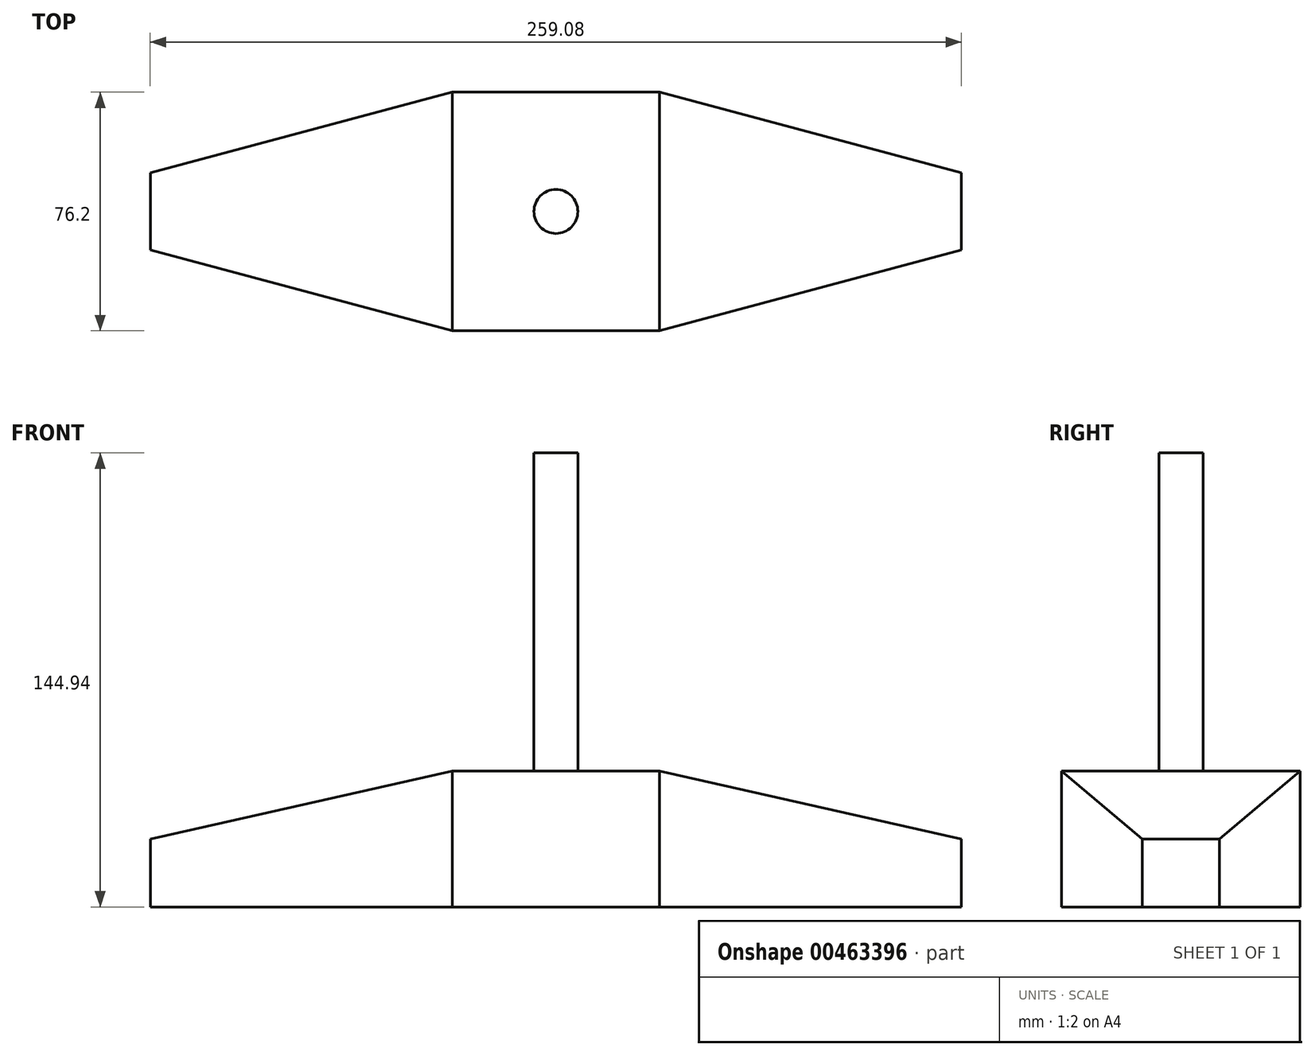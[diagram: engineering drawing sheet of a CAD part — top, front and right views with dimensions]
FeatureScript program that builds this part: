
annotation { "Feature Type Name" : "Feature", "Feature Type Description" : "" }
export const myFeature = defineFeature(function(context is Context, id is Id, definition is map)
    precondition{}
    {
        {
            var Q0;
            Q0=qCreatedBy(makeId("Front.planeOp"),FACE);
            var sketch = newSketch(context, id + "F0", { "sketchPlane" : qUnion([Q0])});
            skLineSegment(sketch, "E0.bottom", {"start": v(33.12, 21.67) * mm, "end": v(-33.12, 21.67) * mm});
            skLineSegment(sketch, "E0.top", {"start": v(129.54, -21.67) * mm, "end": v(-129.54, -21.67) * mm});
            skLineSegment(sketch, "E0.left", {"start": v(129.54, 0) * mm, "end": v(129.54, -21.67) * mm});
            skLineSegment(sketch, "E0.right", {"start": v(-129.54, 0) * mm, "end": v(-129.54, -21.67) * mm});
            skPoint(sketch, "E0.middle", {"position": v(0, 0) * mm});
            skLineSegment(sketch, "E1", {"start": v(-129.54, 0) * mm, "end": v(-33.12, 21.67) * mm});
            skLineSegment(sketch, "E2.MirrorCS", {"start": v(129.54, 0) * mm, "end": v(33.12, 21.67) * mm});
            skPoint(sketch, "E3.orphan", {"position": v(-129.54, 21.67) * mm});
            skPoint(sketch, "E4.orphan", {"position": v(129.54, 21.67) * mm});
            skLineSegment(sketch, "E5.bottom", {"start": v(0, 21.67) * mm, "end": v(14.6, 21.67) * mm});
            skLineSegment(sketch, "E5.top", {"start": v(0, 95.7) * mm, "end": v(14.6, 95.7) * mm});
            skLineSegment(sketch, "E5.left", {"start": v(0, 21.67) * mm, "end": v(0, 95.7) * mm});
            skLineSegment(sketch, "E5.right", {"start": v(14.6, 21.67) * mm, "end": v(14.6, 95.7) * mm});
            skSolve(sketch);
        }
        {
            var Q0;
            Q0=makeQuery(id+"F0.imprint","IMPRINT",FACE,{"disambiguationData":[TD([[makeQuery(id+"F0.imprint","IMPRINT",EDGE,{"derivedFrom":sQuery(id+"F0.wireOp",EDGE,"E0.top")}),-1.0]])]});
            extrude(context, id + "F1", {"entities" : qUnion([Q0]), "depth" : 76.2 * mm});
        }
        {
            var Q0;
            Q0=makeQuery(id+"F1.opExtrude","SWEPT_FACE",FACE,{"disambiguationData":[OSD([sQuery(id+"F0.wireOp",EDGE,"E0.bottom"),sQuery(id+"F0.wireOp",EDGE,"E5.bottom")])]});
            var sketch = newSketch(context, id + "F2", { "sketchPlane" : qUnion([Q0])});
            skPoint(sketch, "E6", {"position": v(0, -38.1) * mm});
            skPoint(sketch, "E6.positionSnap0", {"position": v(-33.12, -38.1) * mm});
            skPoint(sketch, "E6.positionSnap1", {"position": v(0, -76.2) * mm});
            skCircle(sketch, "E7", {"center": v(0, -38.1) * mm, "radius": 7.01 * mm});
            skSolve(sketch);
        }
        {
            var Q0;
            Q0=makeQuery(id+"F2.imprint","IMPRINT",FACE,{"disambiguationData":[TD([[makeQuery(id+"F2.imprint","IMPRINT",EDGE,{"derivedFrom":sQuery(id+"F2.wireOp",EDGE,"E7")}),1.0]])]});
            extrude(context, id + "F3", {"entities" : qUnion([Q0]), "operationType" : NewBodyOperationType.ADD, "depth" : 101.6 * mm});
        }
        {
            var Q0;
            Q0=makeQuery(id+"F1.opExtrude","SWEPT_FACE",FACE,{"disambiguationData":[OSD([sQuery(id+"F0.wireOp",EDGE,"E0.bottom"),sQuery(id+"F0.wireOp",EDGE,"E5.bottom")])]});
            var sketch = newSketch(context, id + "F4", { "sketchPlane" : qUnion([Q0])});
            skLineSegment(sketch, "E8", {"start": v(33.12, 0) * mm, "end": v(134.8, -27.2) * mm});
            skLineSegment(sketch, "E9", {"start": v(134.8, -27.2) * mm, "end": v(134.8, 6.29) * mm});
            skLineSegment(sketch, "E10", {"start": v(134.8, 6.29) * mm, "end": v(33.12, 0) * mm});
            skLineSegment(sketch, "E11.MirrorCS", {"start": v(-33.12, 0) * mm, "end": v(-134.8, -27.2) * mm});
            skLineSegment(sketch, "E12.MirrorCS", {"start": v(-134.8, 6.29) * mm, "end": v(-33.12, 0) * mm});
            skLineSegment(sketch, "E13.MirrorCS", {"start": v(-134.8, -27.2) * mm, "end": v(-134.8, 6.29) * mm});
            skLineSegment(sketch, "E14.MirrorCS", {"start": v(33.12, -76.2) * mm, "end": v(134.8, -49) * mm});
            skLineSegment(sketch, "E15.MirrorCS", {"start": v(134.8, -82.49) * mm, "end": v(33.12, -76.2) * mm});
            skLineSegment(sketch, "E16.MirrorCS", {"start": v(134.8, -49) * mm, "end": v(134.8, -82.49) * mm});
            skLineSegment(sketch, "E17.MirrorCS", {"start": v(-33.12, -76.2) * mm, "end": v(-134.8, -49) * mm});
            skLineSegment(sketch, "E18.MirrorCS", {"start": v(-134.8, -82.49) * mm, "end": v(-33.12, -76.2) * mm});
            skLineSegment(sketch, "E19.MirrorCS", {"start": v(-134.8, -49) * mm, "end": v(-134.8, -82.49) * mm});
            skSolve(sketch);
        }
        {
            var Q0;
            Q0=makeQuery(id+"F4.imprint","IMPRINT",FACE,{"disambiguationData":[TD([[makeQuery(id+"F4.imprint","IMPRINT",EDGE,{"derivedFrom":sQuery(id+"F4.wireOp",EDGE,"E8")}),1.0]])]});
            extrude(context, id + "F5", {"entities" : qUnion([Q0]), "operationType" : NewBodyOperationType.REMOVE, "oppositeDirection" : true, "depth" : 76.2 * mm});
        }
        {
            var Q0;
            Q0 = qSketchRegion(id + "F4", true);
            extrude(context, id + "F6", {"entities" : qUnion([Q0]), "operationType" : NewBodyOperationType.REMOVE, "oppositeDirection" : true, "depth" : 76.2 * mm});
        }
    });
